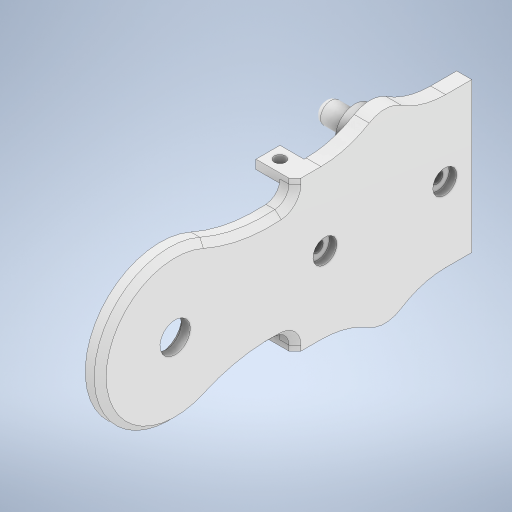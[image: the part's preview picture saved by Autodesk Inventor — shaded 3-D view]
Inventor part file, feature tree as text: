
AUTODESK INVENTOR PART (.ipt)
format: ipt  version: 2024.2 (Build 282272000, 272)  size: 450,560 bytes
history: native  units: in
note: dims shown in document units (in); Inventor stores cm internally (conversion verified against a paired STEP export)
features: extrude x8, sketch x3, fillet x3, chamfer x1, mirror x1
ambient origin geometry x8: Origin, YZ Plane, XZ Plane, XY Plane, X Axis, Y Axis, Z Axis, Center Point
bodies: Solid1 (feature_tree)
feature tree (16):
  sketch  "Sketch1"  dims[d0=0.15in d1=0.15in]
  extrude  "Extrusion1"  Depth=0.15in
  fillet  "Face Fillet1"
  fillet  "Face Fillet2"
  extrude  "Extrusion16"  Depth=0.3937in
  extrude  "Extrusion17"  Depth=0.3937in
  extrude  "Extrusion11"  Depth=0.3937in
  extrude  "Extrusion19"  Depth=1.9685in
  extrude  "Extrusion20"  Depth=0.0197in
  fillet  "Fillet4"  Radius=0.3937in
  chamfer  "Chamfer2"  Distance=0.7874in
  extrude  "Extrusion21"  Depth=0.1969in TaperAngle=0.0deg
  extrude  "Extrusion22"  Depth=0.0197in
  mirror  "Mirror2"
  sketch  "Sketch15"  dims[d2=1.5748in d3=0.3937in]
  sketch  "Sketch16"  dims[d5=0.3543in d7=0.3937in d8=0.3937in d9=1.9685in d12=1.1811in d13=0.3937in d14=0.7874in d22=0.1969in d23=0.0in d30=0.8268in d31=0.2756in d32=0.2756in d33=0.7874in d34=0.7874in d38=0.1181in d48=0.5906in d55=0.5906in d56=0.3425in d57=0.3425in d58=0.5906in d66=0.1969in d67=0.1969in d88=0.1181in d134=0.315in d135=0.315in d136=0.0984in d137=0.0in d138=0.5697in d157=0.4in d158=0.3937in d159=0.0in d160=0.0787in d161=0.0in d167=0.5906in d168=0.0in d169=0.1969in d170=0.0in d171=0.0787in d172=0.0787in d173=0.0787in d174=45.0deg d175=0.315in d176=0.1181in d177=0.315in d178=0.0in d179=0.15in d180=0.1575in d181=0.1575in d182=0.315in d183=0.0in d54=0.0in d89=0.0197in d90=0.0344in d91=0.0197in d92=0.0344in]
